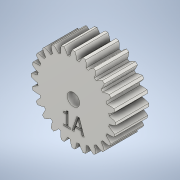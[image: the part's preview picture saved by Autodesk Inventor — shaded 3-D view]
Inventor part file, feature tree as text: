
AUTODESK INVENTOR PART (.ipt)
format: ipt  version: 2021 (Build 250183000, 183)  size: 280,064 bytes
history: native  units: mm (DEFAULTED — no unit token found)
features: sketch x4, plane x3, other x3, extrude x1, hole x1, emboss x1
ambient origin geometry x8: Origin, YZ Plane, XZ Plane, XY Plane, X Axis, Y Axis, Z Axis, Center Point
bodies: Solid1 (feature_tree)
feature tree (13):
  extrude  "Extrusion1"  Depth=8.0mm TaperAngle=0.0deg
  plane  "Work Plane2"
  plane  "Work Plane8"
  plane  "Work Plane9"
  other  "Spur Gear"
  hole  "Hole1"  [1 undecoded]
  emboss  "Emboss1"
  sketch  "Sketch1"  dims[d0=20.48mm d1=8.0mm d2=0.0mm]
  sketch  "Sketch2"  dims[d3=19.2mm d4=10.0mm d5=0.0mm]
  other  "Srf1"
  sketch  "Sketch3"  dims[d16=28.8mm]
  sketch  "Sketch4"  dims[d17=0.0mm d34=1.308997mm d39=0.0mm d41=0.0mm d43=28.8mm d46=28.8mm d47=0.0mm d48=0.0mm d49=3.0mm d50=3.0mm d51=6.0mm d52=4.0mm d53=2.0mm d54=90.0deg d55=8.0mm d56=20.594885mm d57=1.0mm d58=0.0mm]
  other  "Pitch Diameter"
note: 1 required parameter value undecoded (feature->parameter linkage not recoverable at this tier; creation-order binding heuristic only, values carry confidence <= 0.55)
